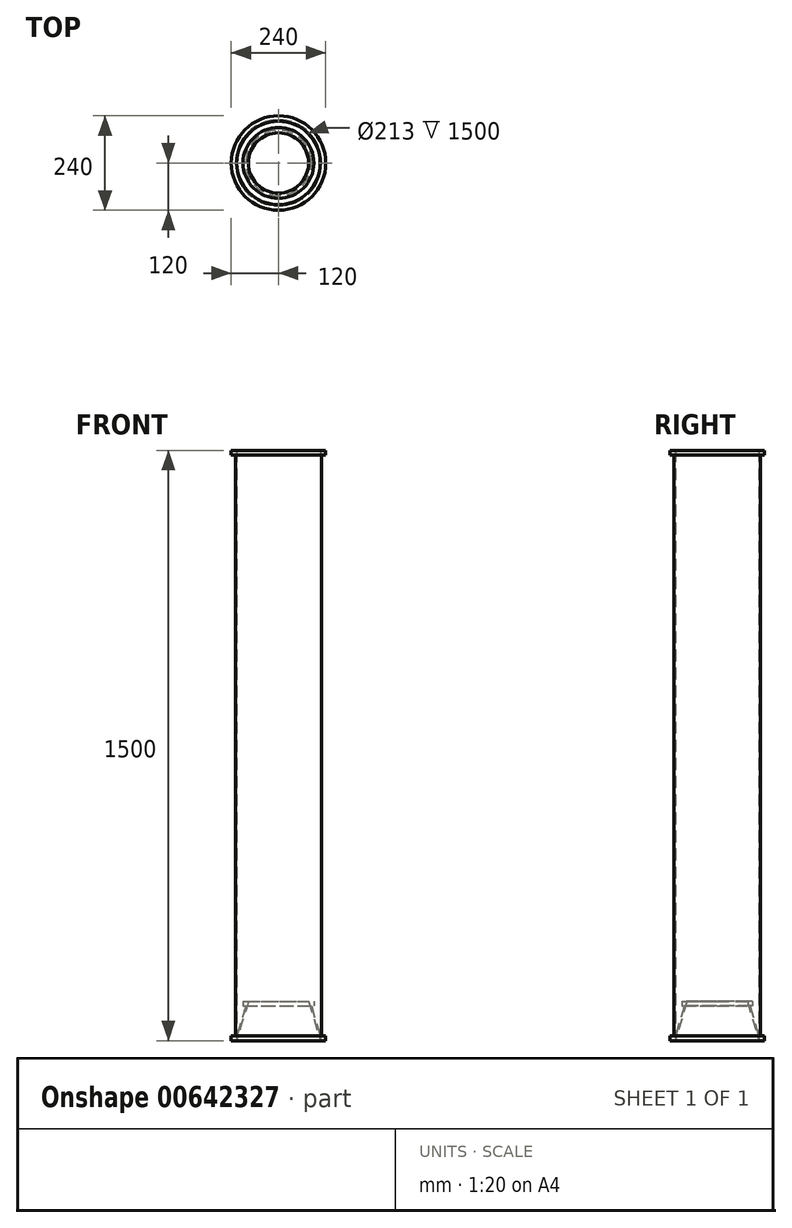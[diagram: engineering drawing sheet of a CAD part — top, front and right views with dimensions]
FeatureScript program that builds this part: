
annotation { "Feature Type Name" : "Feature", "Feature Type Description" : "" }
export const myFeature = defineFeature(function(context is Context, id is Id, definition is map)
    precondition{}
    {
        {
            var Q0;
            Q0=qCreatedBy(makeId("Front.planeOp"),FACE);
            var sketch = newSketch(context, id + "F0", { "sketchPlane" : qUnion([Q0])});
            skLineSegment(sketch, "E0", {"start": v(106.5, 0) * mm, "end": v(120, 0) * mm});
            skLineSegment(sketch, "E1", {"start": v(120, 0) * mm, "end": v(120, 12) * mm});
            skLineSegment(sketch, "E2", {"start": v(120, 12) * mm, "end": v(109.5, 12) * mm});
            skLineSegment(sketch, "E3", {"start": v(109.5, 12) * mm, "end": v(109.5, 1488) * mm});
            skLineSegment(sketch, "E4", {"start": v(109.5, 1488) * mm, "end": v(120, 1488) * mm});
            skLineSegment(sketch, "E5", {"start": v(120, 1488) * mm, "end": v(120, 1500) * mm});
            skLineSegment(sketch, "E6", {"start": v(120, 1500) * mm, "end": v(106.5, 1500) * mm});
            skLineSegment(sketch, "E7", {"start": v(106.5, 1500) * mm, "end": v(106.5, 0) * mm});
            skSolve(sketch);
        }
        {
            var Q0;
            Q0=qCreatedBy(makeId("Front.planeOp"),FACE);
            var sketch = newSketch(context, id + "F1", { "sketchPlane" : qUnion([Q0])});
            skLineSegment(sketch, "E8", {"start": v(0, 0) * mm, "end": v(0, 91.42) * mm, "construction": true});
            skSolve(sketch);
        }
        {
            var Q0;
            Q0 = qSketchRegion(id + "F0", true);
            var Q1;
            Q1=sQuery(id+"F1.wireOp",EDGE,"E8");
            revolve(context, id + "F2", {"entities" : qUnion([Q0]), "axis" : qUnion([Q1]), "revolveType" : RevolveType.FULL});
        }
        {
            var Q0;
            Q0=qCreatedBy(makeId("Front.planeOp"),FACE);
            var sketch = newSketch(context, id + "F3", { "sketchPlane" : qUnion([Q0])});
            skLineSegment(sketch, "E9", {"start": v(106.5, 0) * mm, "end": v(120, 0) * mm});
            skLineSegment(sketch, "E10", {"start": v(120, 0) * mm, "end": v(120, 12) * mm});
            skLineSegment(sketch, "E11", {"start": v(120, 12) * mm, "end": v(106.03, 12) * mm});
            skLineSegment(sketch, "E12", {"start": v(106.03, 12) * mm, "end": v(83.23, 88) * mm});
            skLineSegment(sketch, "E13", {"start": v(83.23, 88) * mm, "end": v(90, 88) * mm});
            skLineSegment(sketch, "E14", {"start": v(90, 88) * mm, "end": v(90, 100) * mm});
            skLineSegment(sketch, "E15", {"start": v(90, 100) * mm, "end": v(76.5, 100) * mm});
            skLineSegment(sketch, "E16", {"start": v(76.5, 100) * mm, "end": v(106.5, 0) * mm});
            skSolve(sketch);
        }
        {
            var Q0;
            Q0 = qSketchRegion(id + "F3", true);
            var Q1;
            Q1=sQuery(id+"F1.wireOp",EDGE,"E8");
            revolve(context, id + "F4", {"entities" : qUnion([Q0]), "axis" : qUnion([Q1]), "revolveType" : RevolveType.FULL});
        }
    });
